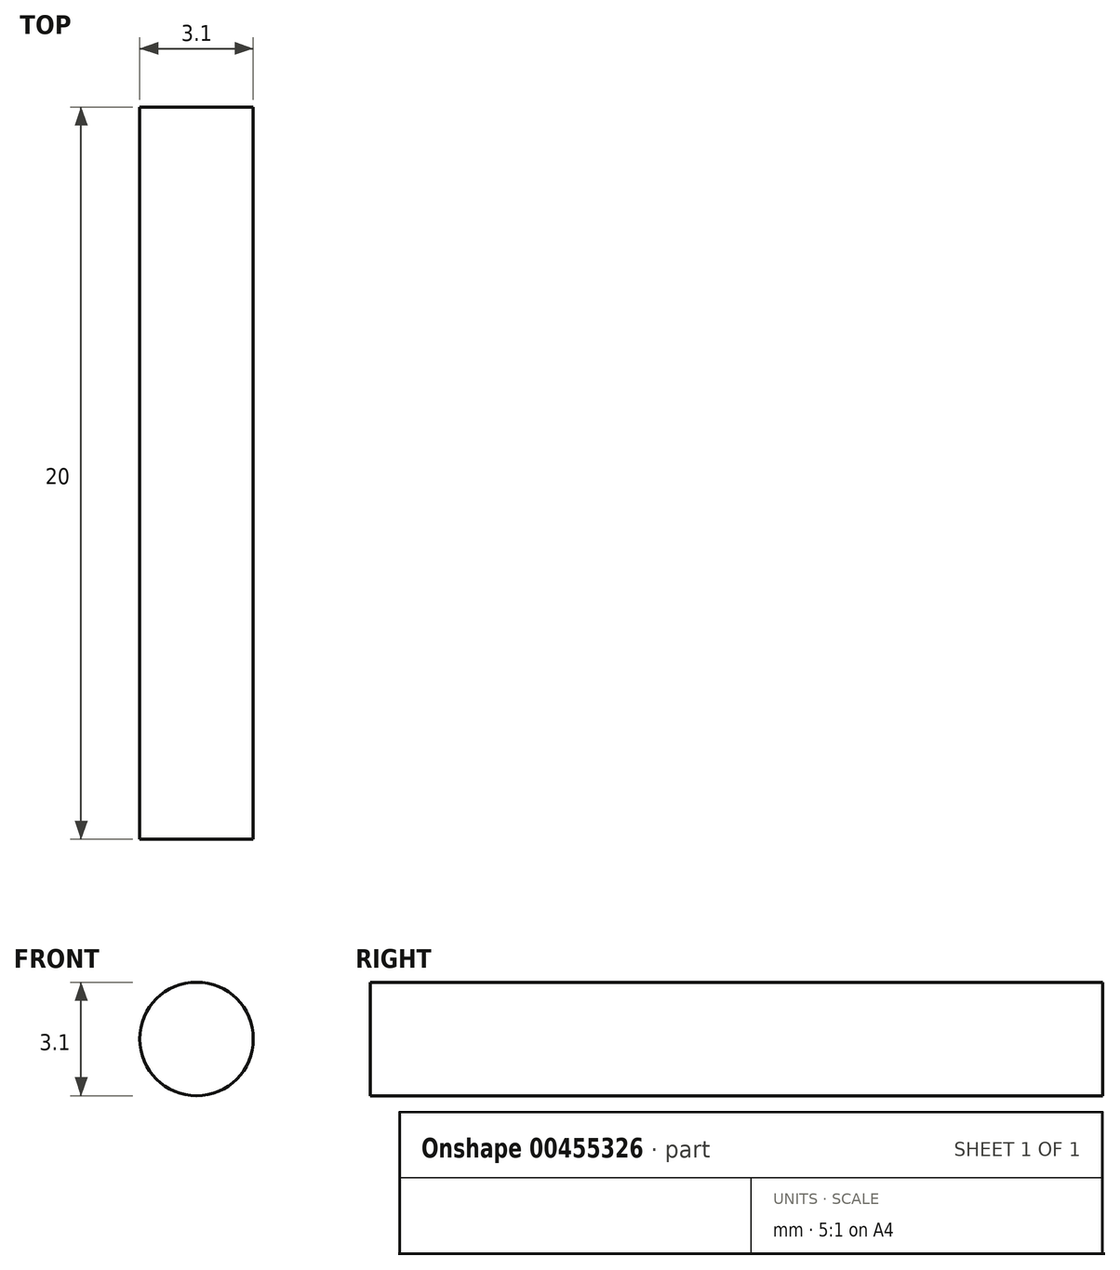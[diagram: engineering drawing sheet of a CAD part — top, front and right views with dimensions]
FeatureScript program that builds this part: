
annotation { "Feature Type Name" : "Feature", "Feature Type Description" : "" }
export const myFeature = defineFeature(function(context is Context, id is Id, definition is map)
    precondition{}
    {
        {
            var Q0;
            Q0=qCreatedBy(makeId("Front.planeOp"),FACE);
            var sketch = newSketch(context, id + "F0", { "sketchPlane" : qUnion([Q0])});
            skCircle(sketch, "E0", {"center": v(0, 0) * mm, "radius": 1.55 * mm});
            skSolve(sketch);
        }
        {
            var Q0;
            Q0=makeQuery(id+"F0.imprint","IMPRINT",FACE,{"disambiguationData":[TD([[makeQuery(id+"F0.imprint","IMPRINT",EDGE,{"derivedFrom":sQuery(id+"F0.wireOp",EDGE,"E0")}),1.0]])]});
            extrude(context, id + "F1", {"entities" : qUnion([Q0]), "endBound" : BoundingType.SYMMETRIC, "depth" : 20 * mm});
        }
    });
